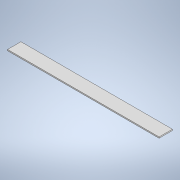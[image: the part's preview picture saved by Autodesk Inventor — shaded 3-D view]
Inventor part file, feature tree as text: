
AUTODESK INVENTOR PART (.ipt)
format: ipt  version: 2020.1 (Build 241239000, 239)  size: 96,256 bytes
history: native  units: mm
features: other x1, extrude x1, sketch x1
ambient origin geometry x8: Origin, YZ Plane, XZ Plane, XY Plane, X Axis, Y Axis, Z Axis, Center Point
bodies: Body1 (feature_tree)
feature tree (3):
  other  "Твердое тело1"
  extrude  "Выдавливание1"  Depth=88.0mm
  sketch  "Эскиз1"
